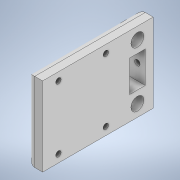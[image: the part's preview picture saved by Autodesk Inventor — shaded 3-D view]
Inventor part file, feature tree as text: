
AUTODESK INVENTOR PART (.ipt)
format: ipt  version: 2022.3 (Build 263350000, 350)  size: 306,688 bytes
history: native  units: mm
features: sketch x6, extrude x3, hole x3, fillet x1, emboss x1
ambient origin geometry x8: Origin, YZ Plane, XZ Plane, XY Plane, X Axis, Y Axis, Z Axis, Center Point
bodies: Solid1 (feature_tree)
feature tree (14):
  extrude  "Extrusion1"  Depth=10.0mm
  sketch  "Sketch2"  dims[d2=50.0mm d3=0.0mm d4=20.0mm]
  extrude  "Extrusion2"  Depth=20.0mm
  extrude  "Extrusion3"  Depth=7.5mm
  hole  "Hole1"  [1 undecoded]
  sketch  "Sketch4"  dims[d7=90.0deg d8=8.2mm d9=12.0mm]
  fillet  "Fillet1"  Radius=12.0mm
  hole  "Hole2"  [1 undecoded]
  hole  "Hole3"  [1 undecoded]
  emboss  "Emboss1"
  sketch  "Sketch1"  dims[d0=10.0mm d1=70.0mm]
  sketch  "Sketch3"  dims[d5=7.5mm d6=7.5mm]
  sketch  "Sketch5"  dims[d10=8.2mm d11=12.0mm]
  sketch  "Sketch6"  dims[d12=10.0mm d13=20.0mm d14=0.0mm d15=0.0mm d16=2.0mm d17=0.0mm d18=10.0mm d19=5.0mm d20=30.0mm d21=40.0mm d22=3.4mm d23=6.0mm d24=5.9mm d25=2.0mm d26=90.0deg d27=1.2mm d28=0.0mm d29=5.0mm d30=5.0mm d31=90.0deg d32=3.4mm d33=6.0mm d34=5.9mm d35=2.0mm d36=90.0deg d37=5.0mm d38=0.0mm d39=3.4mm d40=6.0mm d41=4.1mm d42=5.1mm d43=90.0deg d44=6.9mm d45=0.0mm d46=40.0mm d47=0.0mm d48=50.0mm d49=0.0mm d50=1.0mm d51=0.0mm]
note: 3 required parameter values undecoded (feature->parameter linkage not recoverable at this tier; creation-order binding heuristic only, values carry confidence <= 0.55)
